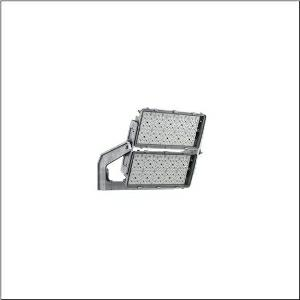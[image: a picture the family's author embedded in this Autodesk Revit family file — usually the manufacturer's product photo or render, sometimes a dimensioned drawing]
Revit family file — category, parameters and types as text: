
# Revit family: floodlight_fl_11_maxi_remote___rs12_5xa779514m01ba_3a09
name_source: partatom
category: Lighting Fixtures
units: mm (PartAtom-declared; Revit-internal decimal feet)

## family parameters
Cut with Voids When Loaded = No
Host = Face
Light Source = No
Part Type = Normal
Room Calculation Point = No
Round Connector Dimension = Use Diameter
Shared = No

## types (1)
- --- (1 x LED, 76660 lm, 707.9 W, 5700K)
    Apparent Load = 708 VA
    CIE Flux Codes = 79 92 99 100 100
    Color Rendering = 90
    Color Temperature = 5700K
    Default Elevation = 1800 mm
    Description = Floodlight FL 11  maxi  Remote floodlight; light control with lens of PMMA; cover panel of toughened safety glass, transparent; light distribution: RS12, rotationally symmetric direct distribution, LEDcolour temperature: 5700K, rated luminous flux: 76.600lm, colour rendering: CRI > 90, light colour: 957; luminous efficacy: 108lm/W; brightness control: DMX+RDM; with terminal, 8-pole, max. 2.5mm², mains connection: 220..240V/380..400V AC, 50/60Hz, surge voltage resistance: line to ground: 10kV, ECG replaceable separately, LED unit replaceable without ESD environment, dustproof LED module, dimming range 10..100%; 708W floodlight with 2x LED unit of diecast aluminium, coated grey; length: 713mm / width: 651mm / height: 338mm; housing frame, of diecast aluminium, uncoated, natural, mounting bracket, of diecast aluminium, uncoated, natural, equipment: Longlife, protection rating (complete): IP66; insulation class (complete): insulation class I (protective earthing); certification: CE, ENEC, VDE; ball protection: ball impact resistance with accessories, only for outdoor installations, rated ambient temperature 10°C, permissible operating ambient temperature: -40..+40°C, permissible storage temperature: -40..+85°C; packaging unit: 1 piece

Light Distribution: RS12
    Height = 320 mm
    Lamp = 1 x LED
    Lamp Light Flux = 76660 lm
    Lamp Power = 707.9 W
    Lamp count = 1
    Length = 712 mm
    Luminous efficacy = 108 lm/W
    Manufacturer = Siteco
    ModVariant = No
    Model = 5XA779514M01BA
    Number of Poles = 1
    OnlyDefault = Yes
    Power Factor = 1
    Product Name = Floodlight FL 11 maxi Remote | RS12
    Product group = floodlight | pylon top
    ProductGroupID = 6101
    Protection Class = Protection class I
    Protection Degree = IP 66
    RLX_Detail_Level = 1
    RlxData = <blob elided: 41061 chars, md5=b0ad9e2e>
    Socket = socket
    Standby Power = 0 W
    System Light Flux = 76660 lm
    System Power = 708 W
    Type Comments = factory setting: luminous flux: 100 % | dim-lin: 254 | 740 mA
    Type Image = l_1006788.jpg
    URL = http://relux.com
    VarID = @adj_095649
    Voltage = 0 V
    Weight = 0.00 kg
    Width = 655 mm

## geometry (parser evidence)
native form markers: Blend x4, Sweep x13
no freeform markers — native parametric forms only
